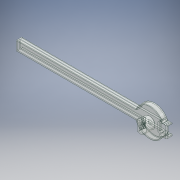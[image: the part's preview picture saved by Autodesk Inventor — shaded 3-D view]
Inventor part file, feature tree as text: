
AUTODESK INVENTOR PART (.ipt)
format: ipt  version: 2018 (Build 220112000, 112)  size: 640,512 bytes
history: native  units: mm
features: sketch x12, extrude x11, projected_geometry x4, fillet x3, mirror x1, shell x1
ambient origin geometry x8: Origin, YZ Plane, XZ Plane, XY Plane, X Axis, Y Axis, Z Axis, Center Point
bodies: 实体1 (feature_tree)
feature tree (32):
  extrude  "拉伸1"  Depth=20.0mm
  extrude  "拉伸2"  Depth=50.0mm
  extrude  "拉伸3"  Depth=17.0mm
  extrude  "拉伸4"  Depth=10.0mm
  extrude  "拉伸5"  Depth=3.0mm TaperAngle=0.0deg
  extrude  "拉伸6"  Depth=20.0mm
  extrude  "拉伸7"  Depth=2.0mm
  sketch  "草图8"  dims[d18=52.0mm d19=4.0mm d20=0.0mm]
  extrude  "拉伸8"  Depth=4.0mm TaperAngle=0.0deg
  extrude  "拉伸9"  Depth=4.0mm TaperAngle=0.0deg
  mirror  "镜像1"
  shell  "抽壳1"  Thickness=6.0mm
  extrude  "拉伸10"  Depth=5.0mm
  extrude  "拉伸11"  Depth=7.0mm TaperAngle=0.0deg
  fillet  "圆角1"  Radius=30.0mm
  fillet  "圆角2"  Radius=26.0mm
  fillet  "圆角3"  Radius=7.0mm
  sketch  "草图1"  dims[d0=20.0mm d1=4.0mm]
  sketch  "草图2"  dims[d2=15.0mm d3=0.0mm d4=50.0mm]
  sketch  "草图3"  dims[d5=17.0mm d6=230.0mm]
  sketch  "草图4"  dims[d7=10.0mm d8=0.0mm d9=245.0mm]
  projected_geometry  "投影回路1"
  sketch  "草图5"  dims[d10=13.0mm d11=3.0mm d12=0.0mm]
  projected_geometry  "投影回路2"
  sketch  "草图6"  dims[d13=20.0mm d14=30.0mm]
  sketch  "草图7"  dims[d15=2.0mm d17=2.0mm]
  projected_geometry  "投影回路5"
  sketch  "草图9"  dims[d21=0.5mm d22=4.0mm d23=2.0mm d24=0.0mm d25=0.0mm d26=6.0mm]
  projected_geometry  "投影回路6"
  sketch  "草图10"  dims[d27=10.75mm d28=0.0mm d30=5.0mm]
  sketch  "草图11"  dims[d31=20.0mm d32=10.75mm d33=0.0mm d34=30.0mm d35=26.0mm d36=7.0mm d37=0.0mm]
  sketch  "草图12"  dims[d38=3.0mm d39=2.5mm d40=2.5mm d41=10.0mm d42=0.0mm d43=1.5mm d44=5.0mm d45=10.0mm d46=0.0mm d47=3.0mm d48=0.5mm d49=5.0mm d50=0.0mm d51=1.0mm d52=1.0mm d53=1.0mm]
